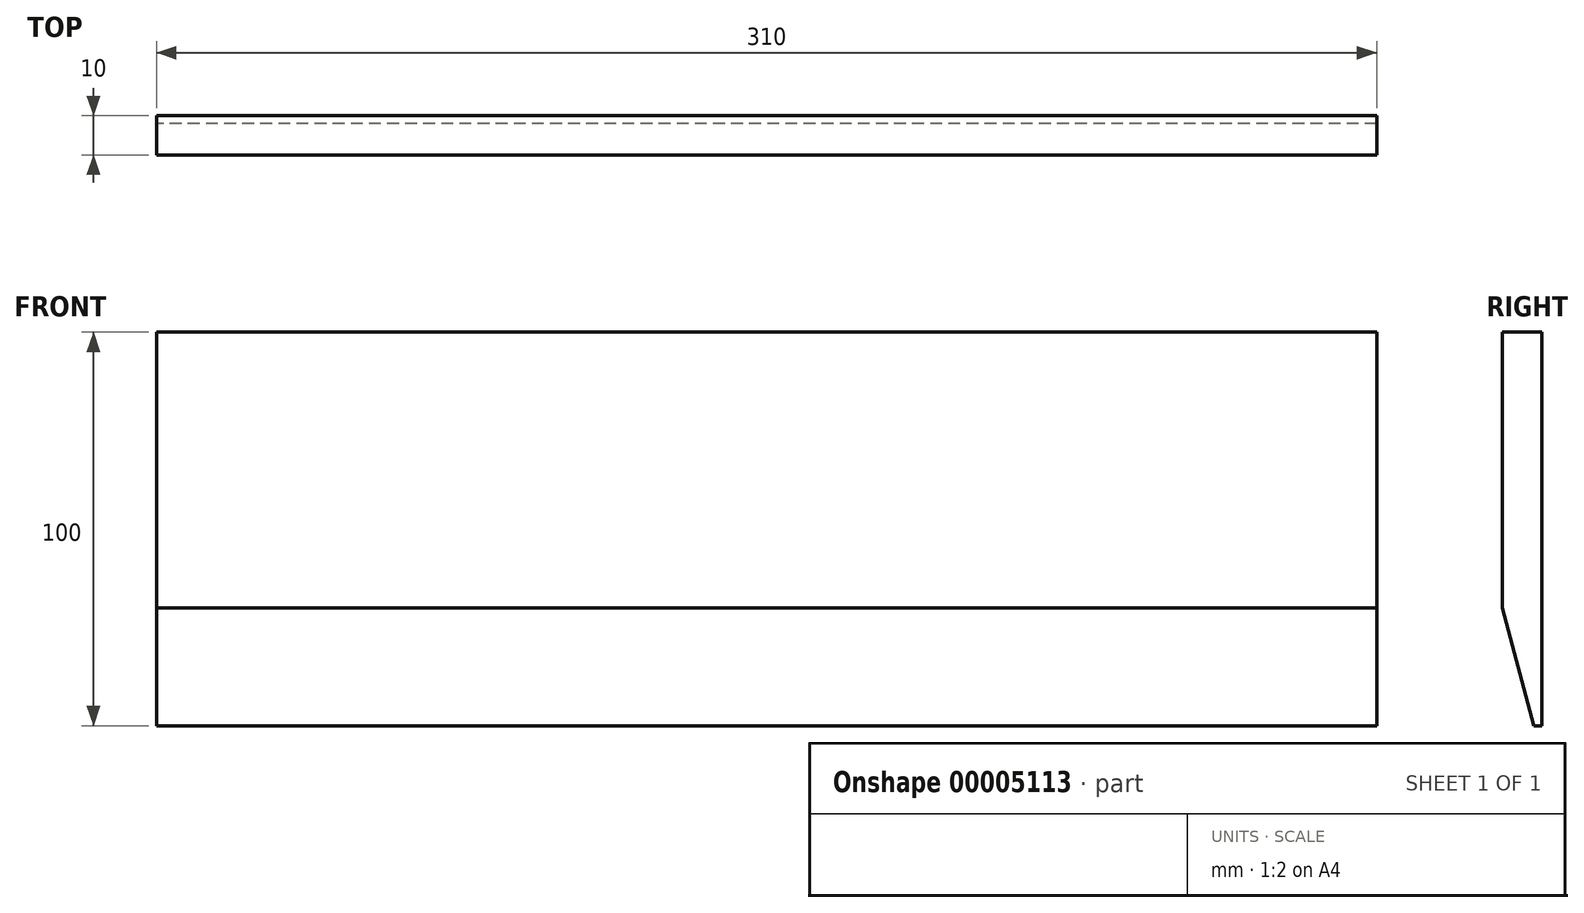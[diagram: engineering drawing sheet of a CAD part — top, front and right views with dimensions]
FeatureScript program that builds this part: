
annotation { "Feature Type Name" : "Feature", "Feature Type Description" : "" }
export const myFeature = defineFeature(function(context is Context, id is Id, definition is map)
    precondition{}
    {
        {
            var Q0;
            Q0=qCreatedBy(makeId("Front.planeOp"),FACE);
            var sketch = newSketch(context, id + "F0", { "sketchPlane" : qUnion([Q0])});
            skLineSegment(sketch, "E0.bottom", {"start": v(-152.38, 87.95) * mm, "end": v(157.62, 87.95) * mm});
            skLineSegment(sketch, "E0.top", {"start": v(-152.38, -12.05) * mm, "end": v(157.62, -12.05) * mm});
            skLineSegment(sketch, "E0.left", {"start": v(-152.38, 87.95) * mm, "end": v(-152.38, -12.05) * mm});
            skLineSegment(sketch, "E0.right", {"start": v(157.62, 87.95) * mm, "end": v(157.62, -12.05) * mm});
            skSolve(sketch);
        }
        {
            var Q0;
            Q0=makeQuery(id+"F0.imprint","IMPRINT",FACE,{"disambiguationData":[TD([[makeQuery(id+"F0.imprint","IMPRINT",EDGE,{"derivedFrom":sQuery(id+"F0.wireOp",EDGE,"E0.bottom")}),-1.0]])]});
            extrude(context, id + "F1", {"entities" : qUnion([Q0]), "depth" : 10 * mm});
        }
        {
            var Q0;
            Q0=makeQuery(id+"F1.opExtrude","CAP_EDGE",EDGE,{"disambiguationData":[OSD([sQuery(id+"F0.wireOp",EDGE,"E0.top")])],"isStart":false});
            chamfer(context, id + "F2", {"entities" : qUnion([Q0]), "chamferType" : ChamferType.TWO_OFFSETS, "width1" : 30 * mm, "oppositeDirection" : false, "width2" : 8 * mm, "tangentPropagation" : true});
        }
    });
